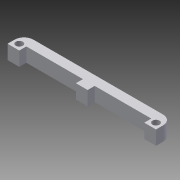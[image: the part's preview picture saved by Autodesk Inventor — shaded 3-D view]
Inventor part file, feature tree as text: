
AUTODESK INVENTOR PART (.ipt)
format: ipt  version: 2013 (Build 170138000, 138)  size: 93,696 bytes
history: native  units: mm
features: extrude x1, sketch x1
ambient origin geometry x8: Origin, YZ Plane, XZ Plane, XY Plane, X Axis, Y Axis, Z Axis, Center Point
bodies: Solid1 (feature_tree)
feature tree (2):
  extrude  "Extrusion1"  [1 undecoded]
  sketch  "Sketch1"  dims[d0=6.0mm d1=0.0mm]
note: 1 required parameter value undecoded (feature->parameter linkage not recoverable at this tier; creation-order binding heuristic only, values carry confidence <= 0.55)
